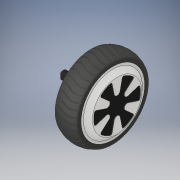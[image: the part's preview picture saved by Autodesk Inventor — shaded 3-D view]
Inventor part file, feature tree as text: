
AUTODESK INVENTOR PART (.ipt)
format: ipt  version: 2019 (Build 230136000, 136)  size: 1,552,896 bytes
history: native  units: mm
features: projected_geometry x2, other x1, extrude x1, sketch x1
ambient origin geometry x8: Origin, YZ Plane, XZ Plane, XY Plane, X Axis, Y Axis, Z Axis, Center Point
bodies: Solid1 (feature_tree)
feature tree (5):
  other  "솔리드1"
  extrude  "돌출1"  Depth=10.0mm TaperAngle=0.0deg
  sketch  "스케치1"
  projected_geometry  "투영된 루프1"
  projected_geometry  "투영된 루프2"
